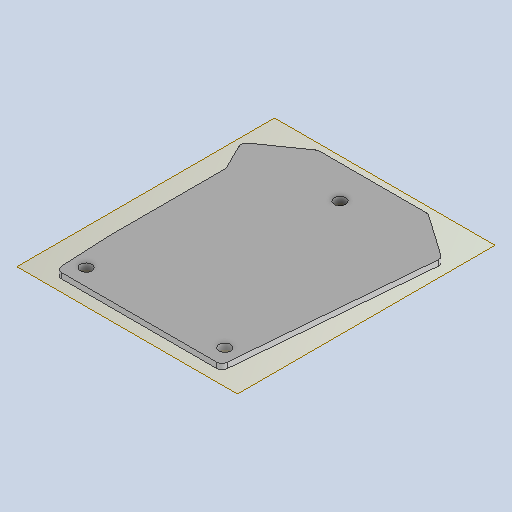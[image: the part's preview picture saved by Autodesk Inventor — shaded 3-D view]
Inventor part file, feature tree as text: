
AUTODESK INVENTOR PART (.ipt)
format: ipt  version: 2025.1 (Build 291241000, 241)  size: 184,320 bytes
history: native  units: mm
features: reference x5, sketch x4, other x3, extrude x2, plane x1, hole x1
ambient origin geometry x8: Origin, YZ Plane, XZ Plane, XY Plane, X Axis, Y Axis, Z Axis, Center Point
bodies: Volumenkörper1 (feature_tree)
feature tree (16):
  plane  "Arbeitsebene1"
  extrude  "Extrusion1"  Depth=2.0mm
  sketch  "Skizze2"  dims[d3=2.0mm d4=0.0mm]
  extrude  "Extrusion2"  [1 undecoded]
  hole  "Bohrung1"  [1 undecoded]
  sketch  "Skizze1"  dims[d0=2.0mm d1=0.0mm d2=0.5mm]
  reference  "Referenz1"
  sketch  "Skizze3"  dims[d5=4.2mm d6=6.0mm d7=4.0mm d8=2.0mm d9=90.0deg d10=8.0mm d11=20.594885mm]
  reference  "Referenz2"
  sketch  "Skizze4"
  reference  "Referenz3"
  reference  "Referenz4"
  reference  "Referenz5"
  other  "<userpath>\OneDrive\Documents\Projekte\Macrolampe\CAD\Baugruppen\Macrolight.iam"
  other  "Macrolight.iam"
  other  "Gehaueseunterteil:1"
note: 2 required parameter values undecoded (feature->parameter linkage not recoverable at this tier; creation-order binding heuristic only, values carry confidence <= 0.55)
